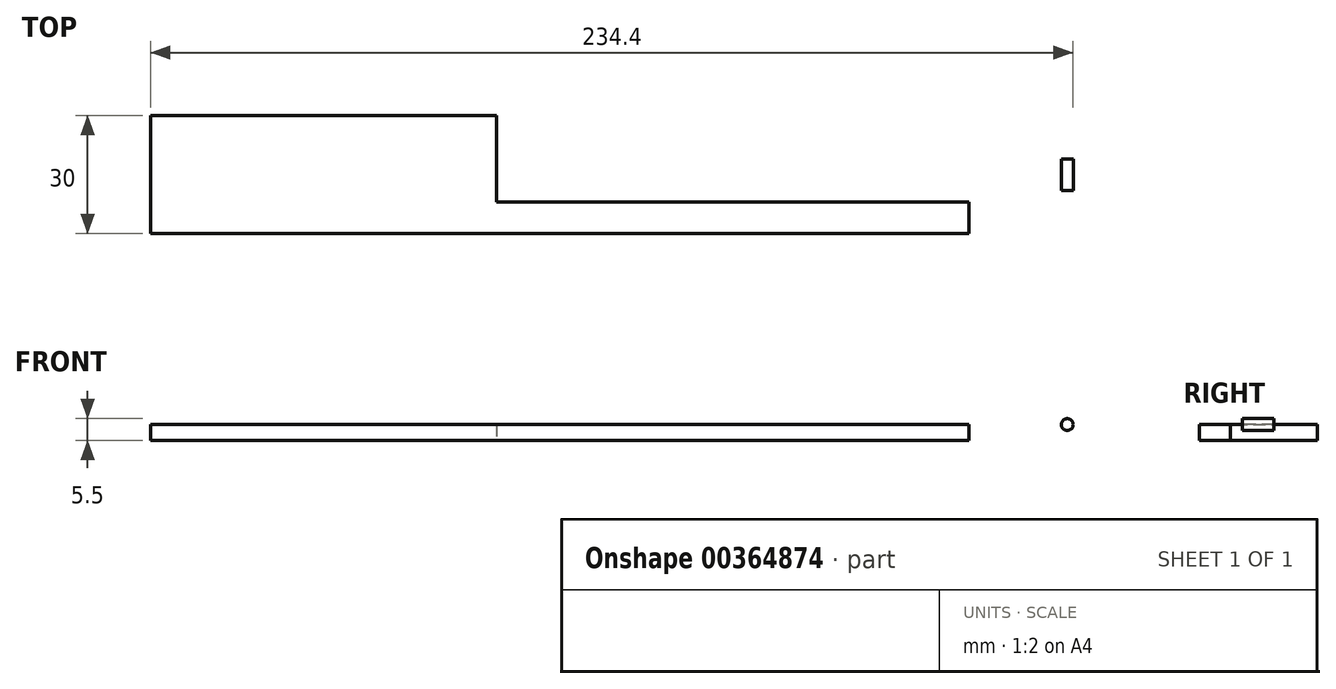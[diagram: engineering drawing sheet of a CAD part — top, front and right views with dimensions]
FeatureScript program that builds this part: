
annotation { "Feature Type Name" : "Feature", "Feature Type Description" : "" }
export const myFeature = defineFeature(function(context is Context, id is Id, definition is map)
    precondition{}
    {
        {
            var Q0;
            Q0=qCreatedBy(makeId("Top.planeOp"),FACE);
            var sketch = newSketch(context, id + "F0", { "sketchPlane" : qUnion([Q0])});
            skLineSegment(sketch, "E0.bottom", {"start": v(83.95, -15) * mm, "end": v(-123.95, -15) * mm});
            skLineSegment(sketch, "E0.top", {"start": v(83.95, 15) * mm, "end": v(-123.95, 15) * mm});
            skLineSegment(sketch, "E0.right", {"start": v(-123.95, -15) * mm, "end": v(-123.95, 15) * mm});
            skPoint(sketch, "E0.middle", {"position": v(0, 0) * mm});
            skLineSegment(sketch, "E1.bottom", {"start": v(83.95, 7) * mm, "end": v(-36.05, 7) * mm});
            skLineSegment(sketch, "E1.top", {"start": v(123.95, 4) * mm, "end": v(-36.05, 4) * mm});
            skLineSegment(sketch, "E1.right", {"start": v(-36.05, 7) * mm, "end": v(-36.05, 4) * mm});
            skLineSegment(sketch, "E2.bottom", {"start": v(123.95, -4) * mm, "end": v(-36.05, -4) * mm});
            skLineSegment(sketch, "E2.top", {"start": v(83.95, -7) * mm, "end": v(-36.05, -7) * mm});
            skLineSegment(sketch, "E2.right", {"start": v(-36.05, -4) * mm, "end": v(-36.05, -7) * mm});
            skLineSegment(sketch, "E3.trimOffspring", {"start": v(123.95, -4) * mm, "end": v(123.95, 4) * mm});
            skLineSegment(sketch, "E4.right", {"start": v(83.95, 15) * mm, "end": v(83.95, 7) * mm});
            skPoint(sketch, "E5.trimOffspring.end.orphan", {"position": v(123.95, 15) * mm});
            skLineSegment(sketch, "E6.right", {"start": v(83.95, -7) * mm, "end": v(83.95, -15) * mm});
            skPoint(sketch, "E7.orphan", {"position": v(123.95, -15) * mm});
            skSolve(sketch);
        }
        {
            var Q0;
            Q0 = qSketchRegion(id + "F0", true);
            extrude(context, id + "F1", {"entities" : qUnion([Q0]), "depth" : 4 * mm});
        }
        {
            var Q0;
            Q0=makeQuery(id+"F1.opExtrude","CAP_FACE",FACE,{"disambiguationData":[OSD([sQuery(id+"F0.wireOp",EDGE,"E0.bottom"),sQuery(id+"F0.wireOp",EDGE,"E0.top"),sQuery(id+"F0.wireOp",EDGE,"E0.right"),sQuery(id+"F0.wireOp",EDGE,"E1.bottom"),sQuery(id+"F0.wireOp",EDGE,"E1.top"),sQuery(id+"F0.wireOp",EDGE,"E1.right"),sQuery(id+"F0.wireOp",EDGE,"E2.bottom"),sQuery(id+"F0.wireOp",EDGE,"E2.top"),sQuery(id+"F0.wireOp",EDGE,"E2.right"),sQuery(id+"F0.wireOp",EDGE,"E3.trimOffspring"),sQuery(id+"F0.wireOp",EDGE,"E4.right"),sQuery(id+"F0.wireOp",EDGE,"E6.right")])],"isStart":false});
            var sketch = newSketch(context, id + "F2", { "sketchPlane" : qUnion([Q0])});
            skLineSegment(sketch, "E8.bottom", {"start": v(123.95, 4) * mm, "end": v(84.13, 4) * mm});
            skLineSegment(sketch, "E8.top", {"start": v(123.95, -4) * mm, "end": v(84.13, -4) * mm});
            skLineSegment(sketch, "E8.left", {"start": v(123.95, 4) * mm, "end": v(123.95, -4) * mm});
            skLineSegment(sketch, "E8.right", {"start": v(84.13, 4) * mm, "end": v(84.13, -4) * mm});
            skSolve(sketch);
        }
        {
            var Q0;
            Q0 = qSketchRegion(id + "F2", true);
            extrude(context, id + "F3", {"entities" : qUnion([Q0]), "operationType" : NewBodyOperationType.ADD, "depth" : 4 * mm});
        }
        {
            var Q0;
            Q0=makeQuery(id+"F3.boolean.opBoolean","MERGE",FACE,{"derivedFrom":[makeQuery(id+"F1.opExtrude","SWEPT_FACE",FACE,{"disambiguationData":[OSD([sQuery(id+"F0.wireOp",EDGE,"E2.bottom")])]}),makeQuery(id+"F3.opExtrude","SWEPT_FACE",FACE,{"disambiguationData":[OSD([sQuery(id+"F2.wireOp",EDGE,"E8.top")])]})]});
            var sketch = newSketch(context, id + "F4", { "sketchPlane" : qUnion([Q0])});
            skLineSegment(sketch, "E9.bottom", {"start": v(123.95, 8) * mm, "end": v(108.95, 8) * mm});
            skLineSegment(sketch, "E9.top", {"start": v(123.95, 0) * mm, "end": v(108.95, 0) * mm});
            skLineSegment(sketch, "E9.left", {"start": v(123.95, 8) * mm, "end": v(123.95, 0) * mm});
            skLineSegment(sketch, "E9.right", {"start": v(108.95, 8) * mm, "end": v(108.95, 0) * mm});
            skCircle(sketch, "E10", {"center": v(108.95, 4) * mm, "radius": 1.5 * mm});
            skSolve(sketch);
        }
        {
            var Q0;
            {var subQ0=sQuery(id+"F4.wireOp",EDGE,"E10");var subQ1=sQuery(id+"F4.wireOp",EDGE,"E9.right");var subQ2=makeQuery(id+"F4.imprint","INTERSECT",VERTEX,{"disambiguationData":[OD(0.0)],"derivedFrom":[subQ1,subQ0]});Q0=makeQuery(id+"F4.imprint","IMPRINT",FACE,{"disambiguationData":[TD([[makeQuery(id+"F4.imprint","IMPRINT",EDGE,{"disambiguationData":[TD([[subQ2,-1.0]])],"derivedFrom":subQ1}),1.0]])]});}
            var Q1;
            {var subQ0=sQuery(id+"F4.wireOp",EDGE,"E10");var subQ1=sQuery(id+"F4.wireOp",EDGE,"E9.right");var subQ2=makeQuery(id+"F4.imprint","INTERSECT",VERTEX,{"disambiguationData":[OD(0.0)],"derivedFrom":[subQ1,subQ0]});Q1=makeQuery(id+"F4.imprint","IMPRINT",FACE,{"disambiguationData":[TD([[makeQuery(id+"F4.imprint","IMPRINT",EDGE,{"disambiguationData":[TD([[subQ2,-1.0]])],"derivedFrom":subQ1}),-1.0]])]});}
            var Q2;
            Q2=sQuery(id+"F4.wireOp",EDGE,"E10");
            extrude(context, id + "F5", {"entities" : qUnion([Q0, Q1]), "operationType" : NewBodyOperationType.REMOVE, "surfaceEntities" : qUnion([Q2]), "oppositeDirection" : true, "depth" : 58.8 * mm});
        }
    });
